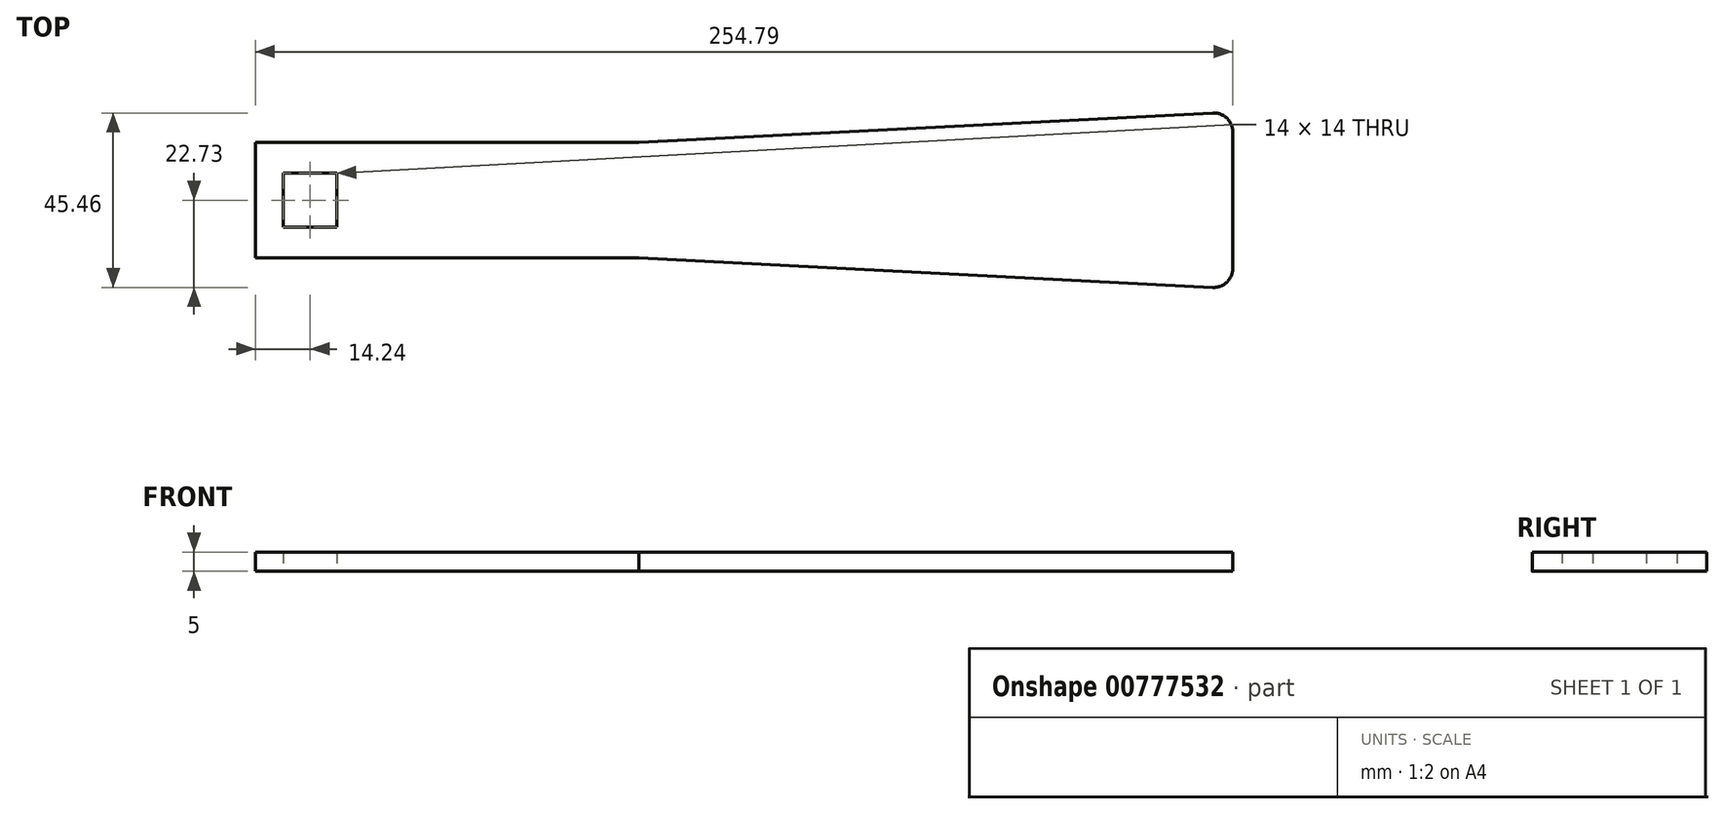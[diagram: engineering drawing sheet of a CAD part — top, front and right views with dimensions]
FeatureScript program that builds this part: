
annotation { "Feature Type Name" : "Feature", "Feature Type Description" : "" }
export const myFeature = defineFeature(function(context is Context, id is Id, definition is map)
    precondition{}
    {
        {
            var Q0;
            Q0=qCreatedBy(makeId("Top.planeOp"),FACE);
            var sketch = newSketch(context, id + "F0", { "sketchPlane" : qUnion([Q0])});
            skLineSegment(sketch, "E0", {"start": v(0, 0) * mm, "end": v(0, 15) * mm});
            skLineSegment(sketch, "E1", {"start": v(0, 15) * mm, "end": v(100, 15) * mm});
            skLineSegment(sketch, "E2", {"start": v(100, 15) * mm, "end": v(254.8, 23) * mm});
            skLineSegment(sketch, "E3", {"start": v(254.8, 23) * mm, "end": v(254.8, 0) * mm});
            skLineSegment(sketch, "E4.MirrorCS", {"start": v(0, 0) * mm, "end": v(0, -15) * mm});
            skLineSegment(sketch, "E5.MirrorCS", {"start": v(0, -15) * mm, "end": v(100, -15) * mm});
            skLineSegment(sketch, "E6.MirrorCS", {"start": v(100, -15) * mm, "end": v(254.8, -23) * mm});
            skLineSegment(sketch, "E7.MirrorCS", {"start": v(254.8, -23) * mm, "end": v(254.8, 0) * mm});
            skSolve(sketch);
        }
        {
            var Q0;
            Q0=makeQuery(id+"F0.imprint","IMPRINT",FACE,{"disambiguationData":[TD([[makeQuery(id+"F0.imprint","IMPRINT",EDGE,{"derivedFrom":sQuery(id+"F0.wireOp",EDGE,"E0")}),-1.0]])]});
            extrude(context, id + "F1", {"entities" : qUnion([Q0]), "depth" : 5 * mm, "offsetDistance" : 25 * mm});
        }
        {
            var Q0;
            Q0=qCreatedBy(makeId("Top.planeOp"),FACE);
            var sketch = newSketch(context, id + "F2", { "sketchPlane" : qUnion([Q0])});
            skLineSegment(sketch, "E8.bottom", {"start": v(7.24, 7) * mm, "end": v(21.24, 7) * mm});
            skLineSegment(sketch, "E8.top", {"start": v(7.24, -7) * mm, "end": v(21.24, -7) * mm});
            skLineSegment(sketch, "E8.left", {"start": v(7.24, 7) * mm, "end": v(7.24, -7) * mm});
            skLineSegment(sketch, "E8.right", {"start": v(21.24, 7) * mm, "end": v(21.24, -7) * mm});
            skSolve(sketch);
        }
        {
            var Q0;
            Q0 = qSketchRegion(id + "F2", true);
            extrude(context, id + "F3", {"entities" : qUnion([Q0]), "operationType" : NewBodyOperationType.REMOVE, "endBound" : BoundingType.UP_TO_NEXT, "depth" : 25 * mm, "offsetDistance" : 25 * mm});
        }
        {
            var Q0;
            Q0=makeQuery(id+"F1.opExtrude","SWEPT_EDGE",EDGE,{"disambiguationData":[OSD([sQuery(id+"F0.wireOp",EDGE,"E6.MirrorCS"),sQuery(id+"F0.wireOp",EDGE,"E7.MirrorCS")])]});
            var Q1;
            Q1=makeQuery(id+"F1.opExtrude","SWEPT_EDGE",EDGE,{"disambiguationData":[OSD([sQuery(id+"F0.wireOp",EDGE,"E2"),sQuery(id+"F0.wireOp",EDGE,"E3")])]});
            fillet(context, id + "F4", {"entities" : qUnion([Q0, Q1]), "radius" : 5 * mm, "tangentPropagation" : true, "allowEdgeOverflow" : false});
        }
    });
